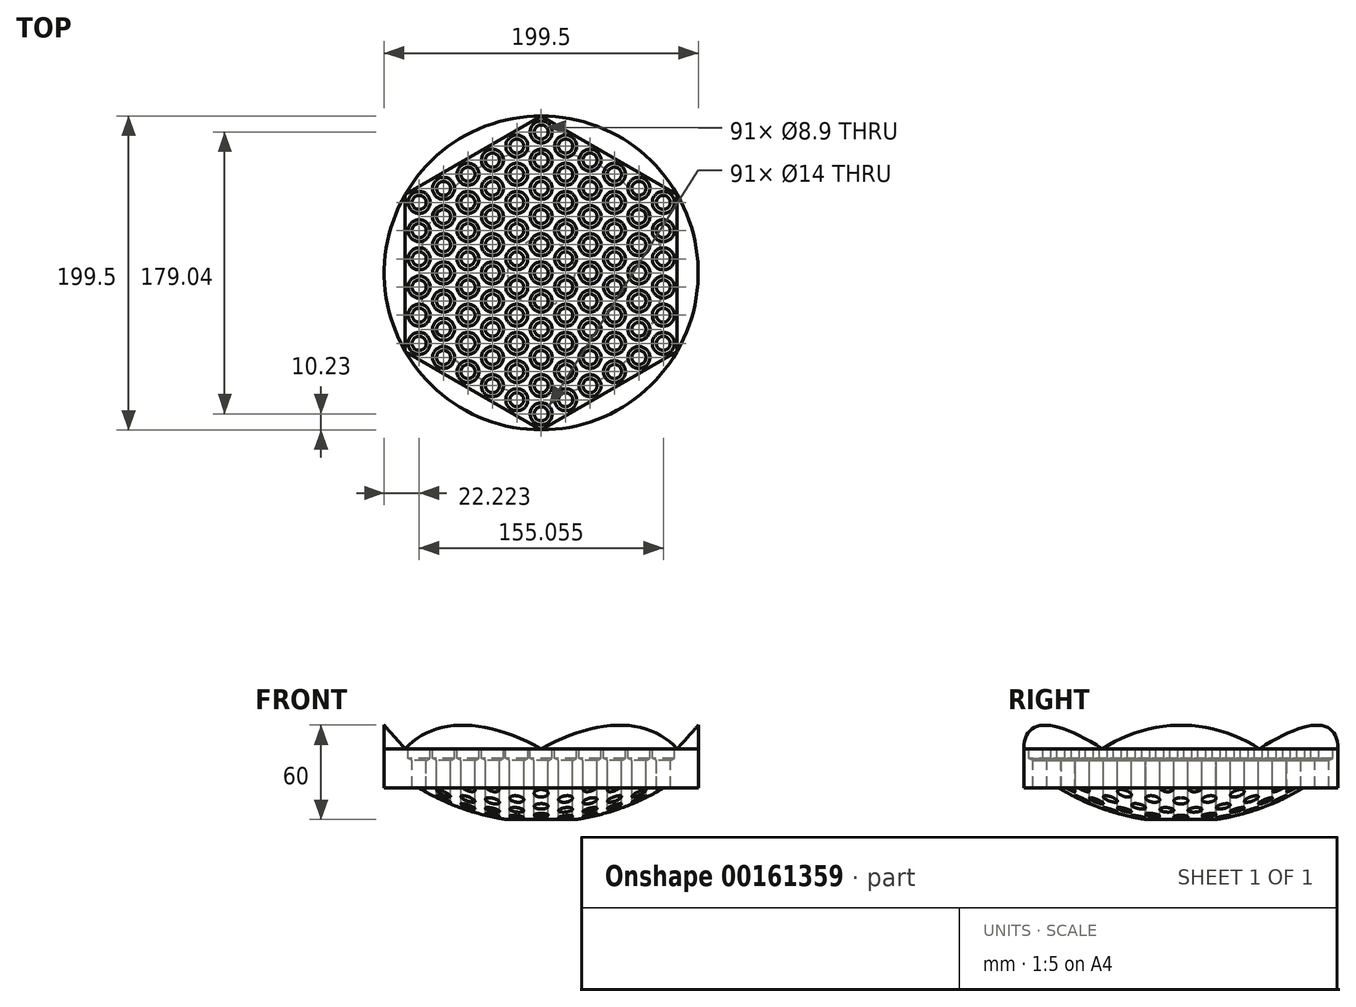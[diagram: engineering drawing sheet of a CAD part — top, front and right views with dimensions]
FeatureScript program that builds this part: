
annotation { "Feature Type Name" : "Feature", "Feature Type Description" : "" }
export const myFeature = defineFeature(function(context is Context, id is Id, definition is map)
    precondition{}
    {
        {
            var Q0;
            Q0=qCreatedBy(makeId("Top.planeOp"),FACE);
            var sketch = newSketch(context, id + "F0", { "sketchPlane" : qUnion([Q0])});
            skCircle(sketch, "E0", {"center": v(0, 0) * mm, "radius": 99.75 * mm});
            skSolve(sketch);
        }
        {
            var Q0;
            Q0=makeQuery(id+"F0.imprint","IMPRINT",FACE,{"disambiguationData":[TD([[makeQuery(id+"F0.imprint","IMPRINT",EDGE,{"derivedFrom":sQuery(id+"F0.wireOp",EDGE,"E0")}),1.0]])]});
            extrude(context, id + "F1", {"entities" : qUnion([Q0]), "oppositeDirection" : true, "depth" : 25 * mm});
        }
        {
            var Q0;
            Q0=qCreatedBy(makeId("Front.planeOp"),FACE);
            var sketch = newSketch(context, id + "F2", { "sketchPlane" : qUnion([Q0])});
            skPoint(sketch, "E1", {"position": v(0, -25) * mm});
            skPoint(sketch, "E2", {"position": v(-77.53, -25) * mm});
            skPoint(sketch, "E3", {"position": v(0, -45) * mm});
            skPoint(sketch, "E4", {"position": v(-21.35, -45) * mm});
            skPoint(sketch, "E5", {"position": v(77.53, -25) * mm});
            skArc(sketch, "E6", {"start": v(-77.53, -25) * mm, "mid": v(-50.44, -37.81) * mm, "end": v(-21.35, -45) * mm});
            skLineSegment(sketch, "E7", {"start": v(-21.35, -45) * mm, "end": v(0, -45) * mm});
            skLineSegment(sketch, "E8", {"start": v(0, -25) * mm, "end": v(0, -45) * mm});
            skLineSegment(sketch, "E9", {"start": v(0, -25) * mm, "end": v(-77.53, -25) * mm});
            skSolve(sketch);
        }
        {
            var Q0;
            Q0=makeQuery(id+"F2.imprint","IMPRINT",FACE,{"disambiguationData":[TD([[makeQuery(id+"F2.imprint","IMPRINT",EDGE,{"derivedFrom":sQuery(id+"F2.wireOp",EDGE,"E6")}),1.0]])]});
            var Q1;
            Q1=sQuery(id+"F2.wireOp",EDGE,"E8");
            revolve(context, id + "F3", {"operationType" : NewBodyOperationType.ADD, "entities" : qUnion([Q0]), "axis" : qUnion([Q1]), "revolveType" : RevolveType.FULL});
        }
        {
            var Q0;
            Q0=makeQuery(id+"F1.opExtrude","CAP_FACE",FACE,{"disambiguationData":[OSD([sQuery(id+"F0.wireOp",EDGE,"E0")])],"isStart":true});
            var sketch = newSketch(context, id + "F4", { "sketchPlane" : qUnion([Q0])});
            skPoint(sketch, "E10", {"position": v(0, 0) * mm});
            skPoint(sketch, "E11.0.1.0", {"position": v(0, 17.9) * mm});
            skPoint(sketch, "E11.0.2.0", {"position": v(0, 35.8) * mm});
            skPoint(sketch, "E11.0.3.0", {"position": v(0, 53.71) * mm});
            skPoint(sketch, "E11.0.4.0", {"position": v(0, 71.62) * mm});
            skPoint(sketch, "E11.0.5.0", {"position": v(0, 89.52) * mm});
            skPoint(sketch, "E11.1.0.0", {"position": v(31.01, 0) * mm});
            skPoint(sketch, "E11.1.1.0", {"position": v(31.01, 17.9) * mm});
            skPoint(sketch, "E11.1.2.0", {"position": v(31.01, 35.8) * mm});
            skPoint(sketch, "E11.1.3.0", {"position": v(31.01, 53.71) * mm});
            skPoint(sketch, "E11.1.4.0", {"position": v(31.01, 71.62) * mm});
            skPoint(sketch, "E11.2.0.0", {"position": v(62.02, 0) * mm});
            skPoint(sketch, "E11.2.1.0", {"position": v(62.02, 17.9) * mm});
            skPoint(sketch, "E11.2.2.0", {"position": v(62.02, 35.8) * mm});
            skPoint(sketch, "E11.2.3.0", {"position": v(62.02, 53.71) * mm});
            skLineSegment(sketch, "E11.direction1", {"start": v(0, 0) * mm, "end": v(31.01, 0) * mm, "construction": true});
            skLineSegment(sketch, "E11.direction2", {"start": v(0, 0) * mm, "end": v(0, 17.9) * mm, "construction": true});
            skPoint(sketch, "E12", {"position": v(15.5, 8.95) * mm});
            skPoint(sketch, "E13.0.1.0", {"position": v(15.5, 26.86) * mm});
            skPoint(sketch, "E13.0.2.0", {"position": v(15.5, 44.76) * mm});
            skPoint(sketch, "E13.0.3.0", {"position": v(15.5, 62.66) * mm});
            skPoint(sketch, "E13.0.4.0", {"position": v(15.5, 80.57) * mm});
            skPoint(sketch, "E13.1.0.0", {"position": v(46.52, 8.95) * mm});
            skPoint(sketch, "E13.1.1.0", {"position": v(46.52, 26.86) * mm});
            skPoint(sketch, "E13.1.2.0", {"position": v(46.52, 44.76) * mm});
            skPoint(sketch, "E13.1.3.0", {"position": v(46.52, 62.66) * mm});
            skPoint(sketch, "E13.2.0.0", {"position": v(77.53, 8.95) * mm});
            skPoint(sketch, "E13.2.1.0", {"position": v(77.53, 26.86) * mm});
            skPoint(sketch, "E13.2.2.0", {"position": v(77.53, 44.76) * mm});
            skLineSegment(sketch, "E13.direction1", {"start": v(15.5, 8.95) * mm, "end": v(46.52, 8.95) * mm, "construction": true});
            skLineSegment(sketch, "E13.direction2", {"start": v(15.5, 8.95) * mm, "end": v(15.5, 26.86) * mm, "construction": true});
            skPoint(sketch, "E14.MirrorP", {"position": v(-15.5, 8.95) * mm});
            skPoint(sketch, "E15.MirrorP", {"position": v(-31.01, 35.8) * mm});
            skPoint(sketch, "E16.MirrorP", {"position": v(-77.53, 26.86) * mm});
            skPoint(sketch, "E17.MirrorP", {"position": v(-77.53, 8.95) * mm});
            skPoint(sketch, "E18.MirrorP", {"position": v(-46.52, 8.95) * mm});
            skPoint(sketch, "E19.MirrorP", {"position": v(-15.5, 80.57) * mm});
            skPoint(sketch, "E20.MirrorP", {"position": v(-15.5, 62.66) * mm});
            skPoint(sketch, "E21.MirrorP", {"position": v(-15.5, 44.76) * mm});
            skPoint(sketch, "E22.MirrorP", {"position": v(-15.5, 26.86) * mm});
            skLineSegment(sketch, "E23.MirrorCS", {"start": v(-15.5, 8.95) * mm, "end": v(-15.5, 26.86) * mm, "construction": true});
            skLineSegment(sketch, "E24.MirrorCS", {"start": v(-15.5, 8.95) * mm, "end": v(-46.52, 8.95) * mm, "construction": true});
            skPoint(sketch, "E25.MirrorP", {"position": v(-62.02, 0) * mm});
            skLineSegment(sketch, "E26.MirrorCS", {"start": v(0, 0) * mm, "end": v(-31.01, 0) * mm, "construction": true});
            skPoint(sketch, "E27.MirrorP", {"position": v(-77.53, 44.76) * mm});
            skPoint(sketch, "E28.MirrorP", {"position": v(-46.52, 44.76) * mm});
            skPoint(sketch, "E29.MirrorP", {"position": v(-31.01, 71.62) * mm});
            skPoint(sketch, "E30.MirrorP", {"position": v(-31.01, 53.71) * mm});
            skPoint(sketch, "E31.MirrorP", {"position": v(-31.01, 0) * mm});
            skPoint(sketch, "E32.MirrorP", {"position": v(-46.52, 26.86) * mm});
            skPoint(sketch, "E33.MirrorP", {"position": v(-62.02, 17.9) * mm});
            skPoint(sketch, "E34.MirrorP", {"position": v(-31.01, 17.9) * mm});
            skPoint(sketch, "E35.MirrorP", {"position": v(-62.02, 35.8) * mm});
            skPoint(sketch, "E36.MirrorP", {"position": v(-62.02, 53.71) * mm});
            skPoint(sketch, "E37.MirrorP", {"position": v(-46.52, 62.66) * mm});
            skPoint(sketch, "E38.MirrorP", {"position": v(0, -53.71) * mm});
            skPoint(sketch, "E39.MirrorP", {"position": v(0, -71.62) * mm});
            skPoint(sketch, "E40.MirrorP", {"position": v(0, -89.52) * mm});
            skPoint(sketch, "E41.MirrorP", {"position": v(0, -17.9) * mm});
            skPoint(sketch, "E42.MirrorP", {"position": v(0, -35.8) * mm});
            skLineSegment(sketch, "E43.MirrorCS", {"start": v(0, 0) * mm, "end": v(0, -17.9) * mm, "construction": true});
            skLineSegment(sketch, "E44.MirrorCS", {"start": v(-15.5, -8.95) * mm, "end": v(-15.5, -26.86) * mm, "construction": true});
            skPoint(sketch, "E45.MirrorP", {"position": v(15.5, -62.66) * mm});
            skPoint(sketch, "E46.MirrorP", {"position": v(77.53, -26.86) * mm});
            skPoint(sketch, "E47.MirrorP", {"position": v(31.01, -53.71) * mm});
            skPoint(sketch, "E48.MirrorP", {"position": v(-62.02, -53.71) * mm});
            skPoint(sketch, "E49.MirrorP", {"position": v(-77.53, -8.95) * mm});
            skPoint(sketch, "E50.MirrorP", {"position": v(15.5, -80.57) * mm});
            skPoint(sketch, "E51.MirrorP", {"position": v(-77.53, -44.76) * mm});
            skPoint(sketch, "E52.MirrorP", {"position": v(77.53, -44.76) * mm});
            skPoint(sketch, "E53.MirrorP", {"position": v(31.01, -71.62) * mm});
            skPoint(sketch, "E54.MirrorP", {"position": v(-31.01, -53.71) * mm});
            skPoint(sketch, "E55.MirrorP", {"position": v(-46.52, -8.95) * mm});
            skPoint(sketch, "E56.MirrorP", {"position": v(62.02, -35.8) * mm});
            skPoint(sketch, "E57.MirrorP", {"position": v(46.52, -8.95) * mm});
            skPoint(sketch, "E58.MirrorP", {"position": v(-15.5, -44.76) * mm});
            skPoint(sketch, "E59.MirrorP", {"position": v(46.52, -62.66) * mm});
            skPoint(sketch, "E60.MirrorP", {"position": v(31.01, -17.9) * mm});
            skPoint(sketch, "E61.MirrorP", {"position": v(-62.02, -17.9) * mm});
            skPoint(sketch, "E62.MirrorP", {"position": v(15.5, -26.86) * mm});
            skPoint(sketch, "E63.MirrorP", {"position": v(-46.52, -44.76) * mm});
            skPoint(sketch, "E64.MirrorP", {"position": v(-15.5, -8.95) * mm});
            skPoint(sketch, "E65.MirrorP", {"position": v(-46.52, -62.66) * mm});
            skPoint(sketch, "E66.MirrorP", {"position": v(-15.5, -80.57) * mm});
            skPoint(sketch, "E67.MirrorP", {"position": v(46.52, -26.86) * mm});
            skPoint(sketch, "E68.MirrorP", {"position": v(-77.53, -26.86) * mm});
            skPoint(sketch, "E69.MirrorP", {"position": v(-62.02, -35.8) * mm});
            skPoint(sketch, "E70.MirrorP", {"position": v(46.52, -44.76) * mm});
            skLineSegment(sketch, "E71.MirrorCS", {"start": v(15.5, -8.95) * mm, "end": v(46.52, -8.95) * mm, "construction": true});
            skPoint(sketch, "E72.MirrorP", {"position": v(15.5, -8.95) * mm});
            skPoint(sketch, "E73.MirrorP", {"position": v(-15.5, -62.66) * mm});
            skPoint(sketch, "E74.MirrorP", {"position": v(-46.52, -26.86) * mm});
            skPoint(sketch, "E75.MirrorP", {"position": v(62.02, -53.71) * mm});
            skPoint(sketch, "E76.MirrorP", {"position": v(31.01, -35.8) * mm});
            skPoint(sketch, "E77.MirrorP", {"position": v(77.53, -8.95) * mm});
            skPoint(sketch, "E78.MirrorP", {"position": v(-15.5, -26.86) * mm});
            skPoint(sketch, "E79.MirrorP", {"position": v(62.02, -17.9) * mm});
            skPoint(sketch, "E80.MirrorP", {"position": v(-31.01, -71.62) * mm});
            skPoint(sketch, "E81.MirrorP", {"position": v(15.5, -44.76) * mm});
            skPoint(sketch, "E82.MirrorP", {"position": v(-31.01, -35.8) * mm});
            skLineSegment(sketch, "E83.MirrorCS", {"start": v(-15.5, -8.95) * mm, "end": v(-46.52, -8.95) * mm, "construction": true});
            skPoint(sketch, "E84.MirrorP", {"position": v(-31.01, -17.9) * mm});
            skLineSegment(sketch, "E85.MirrorCS", {"start": v(15.5, -8.95) * mm, "end": v(15.5, -26.86) * mm, "construction": true});
            skSolve(sketch);
        }
        {
            var Q0;
            Q0=makeQuery(id+"F4.imprint","IMPRINT",FACE,{"disambiguationData":[TD([[makeQuery(id+"F4.imprint","IMPRINT",EDGE,{"derivedFrom":makeQuery(id+"F1.opExtrude","CAP_EDGE",EDGE,{"disambiguationData":[OSD([sQuery(id+"F0.wireOp",EDGE,"E0")])],"isStart":true})}),1.0]])]});
            var sketch = newSketch(context, id + "F5", { "sketchPlane" : qUnion([Q0])});
            skLineSegment(sketch, "E86", {"start": v(86.39, 49.88) * mm, "end": v(86.39, -49.87) * mm});
            skPoint(sketch, "E87", {"position": v(-99.75, 0) * mm});
            skArc(sketch, "E88", {"start": v(86.39, -49.87) * mm, "mid": v(99.75, 0) * mm, "end": v(86.39, 49.88) * mm});
            skSolve(sketch);
        }
        {
            var Q0;
            Q0=makeQuery(id+"F5.imprint","IMPRINT",FACE,{"disambiguationData":[TD([[makeQuery(id+"F5.imprint","IMPRINT",EDGE,{"derivedFrom":sQuery(id+"F5.wireOp",EDGE,"E86")}),1.0]])]});
            extrude(context, id + "F6", {"entities" : qUnion([Q0]), "depth" : 15 * mm});
        }
        {
            var Q0;
            Q0=qCreatedBy(makeId("Front.planeOp"),FACE);
            var sketch = newSketch(context, id + "F7", { "sketchPlane" : qUnion([Q0])});
            skLineSegment(sketch, "E89", {"start": v(86.39, 0) * mm, "end": v(99.75, 15) * mm});
            skLineSegment(sketch, "E90", {"start": v(99.75, 15) * mm, "end": v(86.39, 15) * mm});
            skLineSegment(sketch, "E91", {"start": v(86.39, 15) * mm, "end": v(86.39, 0) * mm});
            skLineSegment(sketch, "E92", {"start": v(0, 0) * mm, "end": v(99.75, 0) * mm});
            skSolve(sketch);
        }
        {
            var Q0;
            Q0 = qSketchRegion(id + "F7", true);
            extrude(context, id + "F8", {"entities" : qUnion([Q0]), "operationType" : NewBodyOperationType.REMOVE, "endBound" : BoundingType.SYMMETRIC, "depth" : 300 * mm});
        }
        {
            var Q0;
            Q0=qCreatedBy(makeId("Front.planeOp"),FACE);
            var sketch = newSketch(context, id + "F9", { "sketchPlane" : qUnion([Q0])});
            skLineSegment(sketch, "E93", {"start": v(0, 71.43) * mm, "end": v(0, -64.48) * mm});
            skSolve(sketch);
        }
        {
            var Q0;
            Q0=makeQuery(id+"F6.opExtrude","SWEPT_BODY",BODY,{"disambiguationData":[OSD([sQuery(id+"F5.wireOp",EDGE,"E86"),sQuery(id+"F5.wireOp",EDGE,"E88")])]});
            var Q1;
            Q1=sQuery(id+"F9.wireOp",EDGE,"E93");
            circularPattern(context, id + "F10", {"entities" : qUnion([Q0]), "axis" : qUnion([Q1]), "angle" : 60 * degree, "instanceCount" : 6});
        }
        {
            var Q0;
            Q0=sQuery(id+"F4.wireOp",VERTEX,"E27.MirrorP");
            var Q1;
            Q1=sQuery(id+"F4.wireOp",VERTEX,"E16.MirrorP");
            var Q2;
            Q2=sQuery(id+"F4.wireOp",VERTEX,"E17.MirrorP");
            var Q3;
            Q3=sQuery(id+"F4.wireOp",VERTEX,"E49.MirrorP");
            var Q4;
            Q4=sQuery(id+"F4.wireOp",VERTEX,"E68.MirrorP");
            var Q5;
            Q5=sQuery(id+"F4.wireOp",VERTEX,"E51.MirrorP");
            var Q6;
            Q6=sQuery(id+"F4.wireOp",VERTEX,"E48.MirrorP");
            var Q7;
            Q7=sQuery(id+"F4.wireOp",VERTEX,"E69.MirrorP");
            var Q8;
            Q8=sQuery(id+"F4.wireOp",VERTEX,"E61.MirrorP");
            var Q9;
            Q9=sQuery(id+"F4.wireOp",VERTEX,"E25.MirrorP");
            var Q10;
            Q10=sQuery(id+"F4.wireOp",VERTEX,"E33.MirrorP");
            var Q11;
            Q11=sQuery(id+"F4.wireOp",VERTEX,"E35.MirrorP");
            var Q12;
            Q12=sQuery(id+"F4.wireOp",VERTEX,"E36.MirrorP");
            var Q13;
            Q13=sQuery(id+"F4.wireOp",VERTEX,"E37.MirrorP");
            var Q14;
            Q14=sQuery(id+"F4.wireOp",VERTEX,"E28.MirrorP");
            var Q15;
            Q15=sQuery(id+"F4.wireOp",VERTEX,"E32.MirrorP");
            var Q16;
            Q16=sQuery(id+"F4.wireOp",VERTEX,"E18.MirrorP");
            var Q17;
            Q17=sQuery(id+"F4.wireOp",VERTEX,"E55.MirrorP");
            var Q18;
            Q18=sQuery(id+"F4.wireOp",VERTEX,"E74.MirrorP");
            var Q19;
            Q19=sQuery(id+"F4.wireOp",VERTEX,"E63.MirrorP");
            var Q20;
            Q20=sQuery(id+"F4.wireOp",VERTEX,"E65.MirrorP");
            var Q21;
            Q21=sQuery(id+"F4.wireOp",VERTEX,"E80.MirrorP");
            var Q22;
            Q22=sQuery(id+"F4.wireOp",VERTEX,"E54.MirrorP");
            var Q23;
            Q23=sQuery(id+"F4.wireOp",VERTEX,"E82.MirrorP");
            var Q24;
            Q24=sQuery(id+"F4.wireOp",VERTEX,"E84.MirrorP");
            var Q25;
            Q25=sQuery(id+"F4.wireOp",VERTEX,"E31.MirrorP");
            var Q26;
            Q26=sQuery(id+"F4.wireOp",VERTEX,"E34.MirrorP");
            var Q27;
            Q27=sQuery(id+"F4.wireOp",VERTEX,"E15.MirrorP");
            var Q28;
            Q28=sQuery(id+"F4.wireOp",VERTEX,"E30.MirrorP");
            var Q29;
            Q29=sQuery(id+"F4.wireOp",VERTEX,"E29.MirrorP");
            var Q30;
            Q30=sQuery(id+"F4.wireOp",VERTEX,"E19.MirrorP");
            var Q31;
            Q31=sQuery(id+"F4.wireOp",VERTEX,"E20.MirrorP");
            var Q32;
            Q32=sQuery(id+"F4.wireOp",VERTEX,"E21.MirrorP");
            var Q33;
            Q33=sQuery(id+"F4.wireOp",VERTEX,"E22.MirrorP");
            var Q34;
            Q34=sQuery(id+"F4.wireOp",VERTEX,"E14.MirrorP");
            var Q35;
            Q35=sQuery(id+"F4.wireOp",VERTEX,"E64.MirrorP");
            var Q36;
            Q36=sQuery(id+"F4.wireOp",VERTEX,"E78.MirrorP");
            var Q37;
            Q37=sQuery(id+"F4.wireOp",VERTEX,"E58.MirrorP");
            var Q38;
            Q38=sQuery(id+"F4.wireOp",VERTEX,"E73.MirrorP");
            var Q39;
            Q39=sQuery(id+"F4.wireOp",VERTEX,"E66.MirrorP");
            var Q40;
            Q40=sQuery(id+"F4.wireOp",VERTEX,"E40.MirrorP");
            var Q41;
            Q41=sQuery(id+"F4.wireOp",VERTEX,"E39.MirrorP");
            var Q42;
            Q42=sQuery(id+"F4.wireOp",VERTEX,"E38.MirrorP");
            var Q43;
            Q43=sQuery(id+"F4.wireOp",VERTEX,"E42.MirrorP");
            var Q44;
            Q44=sQuery(id+"F4.wireOp",VERTEX,"E41.MirrorP");
            var Q45;
            Q45=sQuery(id+"F4.wireOp",VERTEX,"E10");
            var Q46;
            Q46=sQuery(id+"F4.wireOp",VERTEX,"E11.0.1.0");
            var Q47;
            Q47=sQuery(id+"F4.wireOp",VERTEX,"E11.0.2.0");
            var Q48;
            Q48=sQuery(id+"F4.wireOp",VERTEX,"E11.0.3.0");
            var Q49;
            Q49=sQuery(id+"F4.wireOp",VERTEX,"E11.0.4.0");
            var Q50;
            Q50=sQuery(id+"F4.wireOp",VERTEX,"E11.0.5.0");
            var Q51;
            Q51=sQuery(id+"F4.wireOp",VERTEX,"E13.0.4.0");
            var Q52;
            Q52=sQuery(id+"F4.wireOp",VERTEX,"E13.0.3.0");
            var Q53;
            Q53=sQuery(id+"F4.wireOp",VERTEX,"E13.0.2.0");
            var Q54;
            Q54=sQuery(id+"F4.wireOp",VERTEX,"E13.0.1.0");
            var Q55;
            Q55=sQuery(id+"F4.wireOp",VERTEX,"E12");
            var Q56;
            Q56=sQuery(id+"F4.wireOp",VERTEX,"E72.MirrorP");
            var Q57;
            Q57=sQuery(id+"F4.wireOp",VERTEX,"E62.MirrorP");
            var Q58;
            Q58=sQuery(id+"F4.wireOp",VERTEX,"E81.MirrorP");
            var Q59;
            Q59=sQuery(id+"F4.wireOp",VERTEX,"E45.MirrorP");
            var Q60;
            Q60=sQuery(id+"F4.wireOp",VERTEX,"E50.MirrorP");
            var Q61;
            Q61=sQuery(id+"F4.wireOp",VERTEX,"E53.MirrorP");
            var Q62;
            Q62=sQuery(id+"F4.wireOp",VERTEX,"E47.MirrorP");
            var Q63;
            Q63=sQuery(id+"F4.wireOp",VERTEX,"E76.MirrorP");
            var Q64;
            Q64=sQuery(id+"F4.wireOp",VERTEX,"E60.MirrorP");
            var Q65;
            Q65=sQuery(id+"F4.wireOp",VERTEX,"E11.1.0.0");
            var Q66;
            Q66=sQuery(id+"F4.wireOp",VERTEX,"E11.1.1.0");
            var Q67;
            Q67=sQuery(id+"F4.wireOp",VERTEX,"E11.1.2.0");
            var Q68;
            Q68=sQuery(id+"F4.wireOp",VERTEX,"E11.1.3.0");
            var Q69;
            Q69=sQuery(id+"F4.wireOp",VERTEX,"E11.1.4.0");
            var Q70;
            Q70=sQuery(id+"F4.wireOp",VERTEX,"E13.1.3.0");
            var Q71;
            Q71=sQuery(id+"F4.wireOp",VERTEX,"E13.1.2.0");
            var Q72;
            Q72=sQuery(id+"F4.wireOp",VERTEX,"E13.1.1.0");
            var Q73;
            Q73=sQuery(id+"F4.wireOp",VERTEX,"E13.1.0.0");
            var Q74;
            Q74=sQuery(id+"F4.wireOp",VERTEX,"E57.MirrorP");
            var Q75;
            Q75=sQuery(id+"F4.wireOp",VERTEX,"E67.MirrorP");
            var Q76;
            Q76=sQuery(id+"F4.wireOp",VERTEX,"E70.MirrorP");
            var Q77;
            Q77=sQuery(id+"F4.wireOp",VERTEX,"E59.MirrorP");
            var Q78;
            Q78=sQuery(id+"F4.wireOp",VERTEX,"E75.MirrorP");
            var Q79;
            Q79=sQuery(id+"F4.wireOp",VERTEX,"E56.MirrorP");
            var Q80;
            Q80=sQuery(id+"F4.wireOp",VERTEX,"E79.MirrorP");
            var Q81;
            Q81=sQuery(id+"F4.wireOp",VERTEX,"E11.2.0.0");
            var Q82;
            Q82=sQuery(id+"F4.wireOp",VERTEX,"E11.2.1.0");
            var Q83;
            Q83=sQuery(id+"F4.wireOp",VERTEX,"E11.2.2.0");
            var Q84;
            Q84=sQuery(id+"F4.wireOp",VERTEX,"E11.2.3.0");
            var Q85;
            Q85=sQuery(id+"F4.wireOp",VERTEX,"E13.2.2.0");
            var Q86;
            Q86=sQuery(id+"F4.wireOp",VERTEX,"E13.2.1.0");
            var Q87;
            Q87=sQuery(id+"F4.wireOp",VERTEX,"E13.2.0.0");
            var Q88;
            Q88=sQuery(id+"F4.wireOp",VERTEX,"E77.MirrorP");
            var Q89;
            Q89=sQuery(id+"F4.wireOp",VERTEX,"E46.MirrorP");
            var Q90;
            Q90=sQuery(id+"F4.wireOp",VERTEX,"E52.MirrorP");
            var Q91;
            Q91=makeQuery(id+"F1.opExtrude","SWEPT_BODY",BODY,{"disambiguationData":[OSD([sQuery(id+"F0.wireOp",EDGE,"E0")])]});
            hole(context, id + "F11", {"style" : HoleStyle.SIMPLE, "endStyle" : HoleEndStyle.THROUGH, "holeDiameter" : 8.9 * mm, "locations" : qUnion([Q0, Q1, Q2, Q3, Q4, Q5, Q6, Q7, Q8, Q9, Q10, Q11, Q12, Q13, Q14, Q15, Q16, Q17, Q18, Q19, Q20, Q21, Q22, Q23, Q24, Q25, Q26, Q27, Q28, Q29, Q30, Q31, Q32, Q33, Q34, Q35, Q36, Q37, Q38, Q39, Q40, Q41, Q42, Q43, Q44, Q45, Q46, Q47, Q48, Q49, Q50, Q51, Q52, Q53, Q54, Q55, Q56, Q57, Q58, Q59, Q60, Q61, Q62, Q63, Q64, Q65, Q66, Q67, Q68, Q69, Q70, Q71, Q72, Q73, Q74, Q75, Q76, Q77, Q78, Q79, Q80, Q81, Q82, Q83, Q84, Q85, Q86, Q87, Q88, Q89, Q90]), "scope" : qUnion([Q91]), "isTappedThrough" : true});
        }
        {
            var Q0;
            Q0=sQuery(id+"F4.wireOp",VERTEX,"E27.MirrorP");
            var Q1;
            Q1=sQuery(id+"F4.wireOp",VERTEX,"E16.MirrorP");
            var Q2;
            Q2=sQuery(id+"F4.wireOp",VERTEX,"E17.MirrorP");
            var Q3;
            Q3=sQuery(id+"F4.wireOp",VERTEX,"E49.MirrorP");
            var Q4;
            Q4=sQuery(id+"F4.wireOp",VERTEX,"E68.MirrorP");
            var Q5;
            Q5=sQuery(id+"F4.wireOp",VERTEX,"E51.MirrorP");
            var Q6;
            Q6=sQuery(id+"F4.wireOp",VERTEX,"E48.MirrorP");
            var Q7;
            Q7=sQuery(id+"F4.wireOp",VERTEX,"E69.MirrorP");
            var Q8;
            Q8=sQuery(id+"F4.wireOp",VERTEX,"E61.MirrorP");
            var Q9;
            Q9=sQuery(id+"F4.wireOp",VERTEX,"E25.MirrorP");
            var Q10;
            Q10=sQuery(id+"F4.wireOp",VERTEX,"E33.MirrorP");
            var Q11;
            Q11=sQuery(id+"F4.wireOp",VERTEX,"E35.MirrorP");
            var Q12;
            Q12=sQuery(id+"F4.wireOp",VERTEX,"E36.MirrorP");
            var Q13;
            Q13=sQuery(id+"F4.wireOp",VERTEX,"E37.MirrorP");
            var Q14;
            Q14=sQuery(id+"F4.wireOp",VERTEX,"E28.MirrorP");
            var Q15;
            Q15=sQuery(id+"F4.wireOp",VERTEX,"E32.MirrorP");
            var Q16;
            Q16=sQuery(id+"F4.wireOp",VERTEX,"E18.MirrorP");
            var Q17;
            Q17=sQuery(id+"F4.wireOp",VERTEX,"E55.MirrorP");
            var Q18;
            Q18=sQuery(id+"F4.wireOp",VERTEX,"E74.MirrorP");
            var Q19;
            Q19=sQuery(id+"F4.wireOp",VERTEX,"E63.MirrorP");
            var Q20;
            Q20=sQuery(id+"F4.wireOp",VERTEX,"E65.MirrorP");
            var Q21;
            Q21=sQuery(id+"F4.wireOp",VERTEX,"E80.MirrorP");
            var Q22;
            Q22=sQuery(id+"F4.wireOp",VERTEX,"E54.MirrorP");
            var Q23;
            Q23=sQuery(id+"F4.wireOp",VERTEX,"E82.MirrorP");
            var Q24;
            Q24=sQuery(id+"F4.wireOp",VERTEX,"E84.MirrorP");
            var Q25;
            Q25=sQuery(id+"F4.wireOp",VERTEX,"E31.MirrorP");
            var Q26;
            Q26=sQuery(id+"F4.wireOp",VERTEX,"E34.MirrorP");
            var Q27;
            Q27=sQuery(id+"F4.wireOp",VERTEX,"E15.MirrorP");
            var Q28;
            Q28=sQuery(id+"F4.wireOp",VERTEX,"E30.MirrorP");
            var Q29;
            Q29=sQuery(id+"F4.wireOp",VERTEX,"E29.MirrorP");
            var Q30;
            Q30=sQuery(id+"F4.wireOp",VERTEX,"E19.MirrorP");
            var Q31;
            Q31=sQuery(id+"F4.wireOp",VERTEX,"E20.MirrorP");
            var Q32;
            Q32=sQuery(id+"F4.wireOp",VERTEX,"E21.MirrorP");
            var Q33;
            Q33=sQuery(id+"F4.wireOp",VERTEX,"E22.MirrorP");
            var Q34;
            Q34=sQuery(id+"F4.wireOp",VERTEX,"E14.MirrorP");
            var Q35;
            Q35=sQuery(id+"F4.wireOp",VERTEX,"E64.MirrorP");
            var Q36;
            Q36=sQuery(id+"F4.wireOp",VERTEX,"E78.MirrorP");
            var Q37;
            Q37=sQuery(id+"F4.wireOp",VERTEX,"E58.MirrorP");
            var Q38;
            Q38=sQuery(id+"F4.wireOp",VERTEX,"E73.MirrorP");
            var Q39;
            Q39=sQuery(id+"F4.wireOp",VERTEX,"E66.MirrorP");
            var Q40;
            Q40=sQuery(id+"F4.wireOp",VERTEX,"E11.0.5.0");
            var Q41;
            Q41=sQuery(id+"F4.wireOp",VERTEX,"E11.0.4.0");
            var Q42;
            Q42=sQuery(id+"F4.wireOp",VERTEX,"E11.0.3.0");
            var Q43;
            Q43=sQuery(id+"F4.wireOp",VERTEX,"E11.0.2.0");
            var Q44;
            Q44=sQuery(id+"F4.wireOp",VERTEX,"E11.0.1.0");
            var Q45;
            Q45=sQuery(id+"F4.wireOp",VERTEX,"E10");
            var Q46;
            Q46=sQuery(id+"F4.wireOp",VERTEX,"E41.MirrorP");
            var Q47;
            Q47=sQuery(id+"F4.wireOp",VERTEX,"E42.MirrorP");
            var Q48;
            Q48=sQuery(id+"F4.wireOp",VERTEX,"E38.MirrorP");
            var Q49;
            Q49=sQuery(id+"F4.wireOp",VERTEX,"E39.MirrorP");
            var Q50;
            Q50=sQuery(id+"F4.wireOp",VERTEX,"E40.MirrorP");
            var Q51;
            Q51=sQuery(id+"F4.wireOp",VERTEX,"E50.MirrorP");
            var Q52;
            Q52=sQuery(id+"F4.wireOp",VERTEX,"E45.MirrorP");
            var Q53;
            Q53=sQuery(id+"F4.wireOp",VERTEX,"E81.MirrorP");
            var Q54;
            Q54=sQuery(id+"F4.wireOp",VERTEX,"E62.MirrorP");
            var Q55;
            Q55=sQuery(id+"F4.wireOp",VERTEX,"E72.MirrorP");
            var Q56;
            Q56=sQuery(id+"F4.wireOp",VERTEX,"E12");
            var Q57;
            Q57=sQuery(id+"F4.wireOp",VERTEX,"E13.0.1.0");
            var Q58;
            Q58=sQuery(id+"F4.wireOp",VERTEX,"E13.0.2.0");
            var Q59;
            Q59=sQuery(id+"F4.wireOp",VERTEX,"E13.0.3.0");
            var Q60;
            Q60=sQuery(id+"F4.wireOp",VERTEX,"E13.0.4.0");
            var Q61;
            Q61=sQuery(id+"F4.wireOp",VERTEX,"E11.1.4.0");
            var Q62;
            Q62=sQuery(id+"F4.wireOp",VERTEX,"E11.1.3.0");
            var Q63;
            Q63=sQuery(id+"F4.wireOp",VERTEX,"E11.1.2.0");
            var Q64;
            Q64=sQuery(id+"F4.wireOp",VERTEX,"E11.1.1.0");
            var Q65;
            Q65=sQuery(id+"F4.wireOp",VERTEX,"E11.1.0.0");
            var Q66;
            Q66=sQuery(id+"F4.wireOp",VERTEX,"E60.MirrorP");
            var Q67;
            Q67=sQuery(id+"F4.wireOp",VERTEX,"E76.MirrorP");
            var Q68;
            Q68=sQuery(id+"F4.wireOp",VERTEX,"E47.MirrorP");
            var Q69;
            Q69=sQuery(id+"F4.wireOp",VERTEX,"E53.MirrorP");
            var Q70;
            Q70=sQuery(id+"F4.wireOp",VERTEX,"E59.MirrorP");
            var Q71;
            Q71=sQuery(id+"F4.wireOp",VERTEX,"E70.MirrorP");
            var Q72;
            Q72=sQuery(id+"F4.wireOp",VERTEX,"E67.MirrorP");
            var Q73;
            Q73=sQuery(id+"F4.wireOp",VERTEX,"E57.MirrorP");
            var Q74;
            Q74=sQuery(id+"F4.wireOp",VERTEX,"E13.1.0.0");
            var Q75;
            Q75=sQuery(id+"F4.wireOp",VERTEX,"E13.1.1.0");
            var Q76;
            Q76=sQuery(id+"F4.wireOp",VERTEX,"E13.1.2.0");
            var Q77;
            Q77=sQuery(id+"F4.wireOp",VERTEX,"E13.1.3.0");
            var Q78;
            Q78=sQuery(id+"F4.wireOp",VERTEX,"E11.2.3.0");
            var Q79;
            Q79=sQuery(id+"F4.wireOp",VERTEX,"E11.2.2.0");
            var Q80;
            Q80=sQuery(id+"F4.wireOp",VERTEX,"E11.2.1.0");
            var Q81;
            Q81=sQuery(id+"F4.wireOp",VERTEX,"E11.2.0.0");
            var Q82;
            Q82=sQuery(id+"F4.wireOp",VERTEX,"E79.MirrorP");
            var Q83;
            Q83=sQuery(id+"F4.wireOp",VERTEX,"E56.MirrorP");
            var Q84;
            Q84=sQuery(id+"F4.wireOp",VERTEX,"E75.MirrorP");
            var Q85;
            Q85=sQuery(id+"F4.wireOp",VERTEX,"E52.MirrorP");
            var Q86;
            Q86=sQuery(id+"F4.wireOp",VERTEX,"E46.MirrorP");
            var Q87;
            Q87=sQuery(id+"F4.wireOp",VERTEX,"E77.MirrorP");
            var Q88;
            Q88=sQuery(id+"F4.wireOp",VERTEX,"E13.2.0.0");
            var Q89;
            Q89=sQuery(id+"F4.wireOp",VERTEX,"E13.2.1.0");
            var Q90;
            Q90=sQuery(id+"F4.wireOp",VERTEX,"E13.2.2.0");
            var Q91;
            Q91=makeQuery(id+"F1.opExtrude","SWEPT_BODY",BODY,{"disambiguationData":[OSD([sQuery(id+"F0.wireOp",EDGE,"E0")])]});
            hole(context, id + "F12", {"style" : HoleStyle.SIMPLE, "endStyle" : HoleEndStyle.BLIND, "holeDiameter" : 14 * mm, "holeDepth" : 6 * mm, "locations" : qUnion([Q0, Q1, Q2, Q3, Q4, Q5, Q6, Q7, Q8, Q9, Q10, Q11, Q12, Q13, Q14, Q15, Q16, Q17, Q18, Q19, Q20, Q21, Q22, Q23, Q24, Q25, Q26, Q27, Q28, Q29, Q30, Q31, Q32, Q33, Q34, Q35, Q36, Q37, Q38, Q39, Q40, Q41, Q42, Q43, Q44, Q45, Q46, Q47, Q48, Q49, Q50, Q51, Q52, Q53, Q54, Q55, Q56, Q57, Q58, Q59, Q60, Q61, Q62, Q63, Q64, Q65, Q66, Q67, Q68, Q69, Q70, Q71, Q72, Q73, Q74, Q75, Q76, Q77, Q78, Q79, Q80, Q81, Q82, Q83, Q84, Q85, Q86, Q87, Q88, Q89, Q90]), "scope" : qUnion([Q91])});
        }
    });
